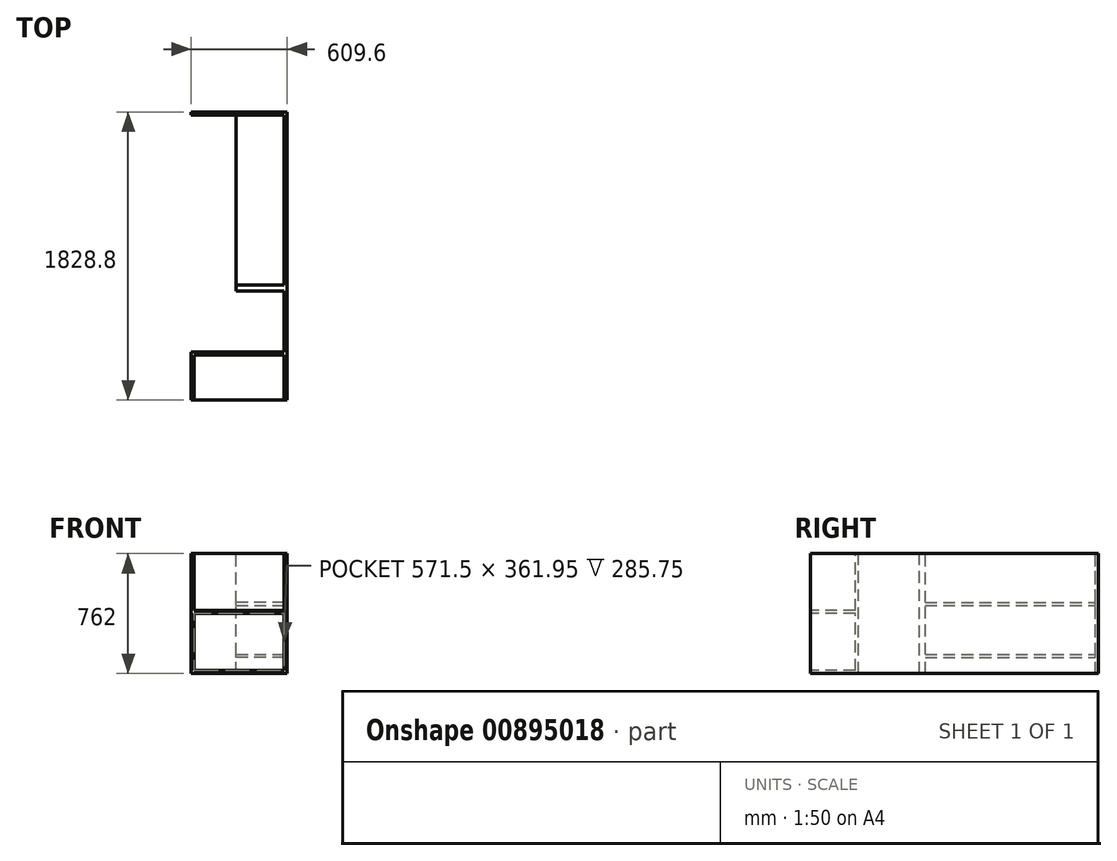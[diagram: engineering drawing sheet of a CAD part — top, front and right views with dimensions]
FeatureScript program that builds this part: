
annotation { "Feature Type Name" : "Feature", "Feature Type Description" : "" }
export const myFeature = defineFeature(function(context is Context, id is Id, definition is map)
    precondition{}
    {
        {
            var Q0;
            Q0=qCreatedBy(makeId("Front.planeOp"),FACE);
            var sketch = newSketch(context, id + "F0", { "sketchPlane" : qUnion([Q0])});
            skLineSegment(sketch, "E0.bottom", {"start": v(304.8, 381) * mm, "end": v(-304.8, 381) * mm});
            skLineSegment(sketch, "E0.top", {"start": v(304.8, -381) * mm, "end": v(-304.8, -381) * mm});
            skLineSegment(sketch, "E0.left", {"start": v(304.8, 381) * mm, "end": v(304.8, -381) * mm});
            skLineSegment(sketch, "E0.right", {"start": v(-304.8, 381) * mm, "end": v(-304.8, -381) * mm});
            skPoint(sketch, "E0.middle", {"position": v(0, 0) * mm});
            skSolve(sketch);
        }
        {
            var Q0;
            Q0=makeQuery(id+"F0.imprint","IMPRINT",FACE,{"disambiguationData":[TD([[makeQuery(id+"F0.imprint","IMPRINT",EDGE,{"derivedFrom":sQuery(id+"F0.wireOp",EDGE,"E0.bottom")}),1.0]])]});
            extrude(context, id + "F1", {"entities" : qUnion([Q0]), "depth" : 304.8 * mm, "offsetDistance" : 25.4 * mm});
        }
        {
            var Q0;
            Q0=makeQuery(id+"F1.opExtrude","CAP_FACE",FACE,{"disambiguationData":[OSD([sQuery(id+"F0.wireOp",EDGE,"E0.bottom"),sQuery(id+"F0.wireOp",EDGE,"E0.top"),sQuery(id+"F0.wireOp",EDGE,"E0.left"),sQuery(id+"F0.wireOp",EDGE,"E0.right")])],"isStart":false});
            var sketch = newSketch(context, id + "F2", { "sketchPlane" : qUnion([Q0])});
            skLineSegment(sketch, "E1.bottom", {"start": v(-285.75, 381) * mm, "end": v(285.75, 381) * mm});
            skLineSegment(sketch, "E1.top", {"start": v(-285.75, 19.05) * mm, "end": v(285.75, 19.05) * mm});
            skLineSegment(sketch, "E1.left", {"start": v(-285.75, 381) * mm, "end": v(-285.75, 19.05) * mm});
            skLineSegment(sketch, "E1.right", {"start": v(285.75, 381) * mm, "end": v(285.75, 19.05) * mm});
            skLineSegment(sketch, "E2.bottom", {"start": v(-285.75, 0) * mm, "end": v(285.75, 0) * mm});
            skLineSegment(sketch, "E2.top", {"start": v(-285.75, -361.95) * mm, "end": v(285.75, -361.95) * mm});
            skLineSegment(sketch, "E2.left", {"start": v(-285.75, 0) * mm, "end": v(-285.75, -361.95) * mm});
            skLineSegment(sketch, "E2.right", {"start": v(285.75, 0) * mm, "end": v(285.75, -361.95) * mm});
            skSolve(sketch);
        }
        {
            var Q0;
            Q0=makeQuery(id+"F2.imprint","IMPRINT",FACE,{"disambiguationData":[TD([[makeQuery(id+"F2.imprint","IMPRINT",EDGE,{"derivedFrom":sQuery(id+"F2.wireOp",EDGE,"E1.bottom")}),-1.0]])]});
            var Q1;
            Q1=makeQuery(id+"F2.imprint","IMPRINT",FACE,{"disambiguationData":[TD([[makeQuery(id+"F2.imprint","IMPRINT",EDGE,{"derivedFrom":sQuery(id+"F2.wireOp",EDGE,"E2.bottom")}),-1.0]])]});
            var Q2;
            Q2=makeQuery(id+"F2.imprint","IMPRINT",FACE,{"disambiguationData":[TD([[makeQuery(id+"F2.imprint","IMPRINT",EDGE,{"derivedFrom":sQuery(id+"F2.wireOp",EDGE,"E1.bottom")}),1.0]])]});
            var Q3;
            Q3=makeQuery(id+"F1.opExtrude","CAP_FACE",FACE,{"disambiguationData":[OSD([sQuery(id+"F0.wireOp",EDGE,"E0.bottom"),sQuery(id+"F0.wireOp",EDGE,"E0.top"),sQuery(id+"F0.wireOp",EDGE,"E0.left"),sQuery(id+"F0.wireOp",EDGE,"E0.right")])],"isStart":true});
            extrude(context, id + "F3", {"entities" : qUnion([Q0, Q1, Q2]), "operationType" : NewBodyOperationType.REMOVE, "endBound" : BoundingType.UP_TO_SURFACE, "oppositeDirection" : true, "depth" : 25.4 * mm, "endBoundEntityFace" : qUnion([Q3]), "hasOffset" : true, "offsetDistance" : 19.05 * mm});
        }
        {
            var Q0;
            Q0=makeQuery(id+"F1.opExtrude","SWEPT_FACE",FACE,{"disambiguationData":[OSD([sQuery(id+"F0.wireOp",EDGE,"E0.bottom")])]});
            var sketch = newSketch(context, id + "F4", { "sketchPlane" : qUnion([Q0])});
            skLineSegment(sketch, "E3", {"start": v(304.8, 0) * mm, "end": v(304.8, 1524) * mm});
            skLineSegment(sketch, "E4", {"start": v(304.8, 1524) * mm, "end": v(-304.8, 1524) * mm});
            skLineSegment(sketch, "E5", {"start": v(-304.8, 1524) * mm, "end": v(-304.8, 1504.95) * mm});
            skLineSegment(sketch, "E6", {"start": v(-304.8, 1504.95) * mm, "end": v(285.75, 1504.95) * mm});
            skLineSegment(sketch, "E7", {"start": v(285.75, 1504.95) * mm, "end": v(285.75, 425.45) * mm});
            skLineSegment(sketch, "E8.bottom", {"start": v(285.75, 387.35) * mm, "end": v(-19.05, 387.35) * mm});
            skLineSegment(sketch, "E8.top", {"start": v(285.75, 425.45) * mm, "end": v(-19.05, 425.45) * mm});
            skLineSegment(sketch, "E8.right", {"start": v(-19.05, 425.45) * mm, "end": v(-19.05, 387.35) * mm});
            skLineSegment(sketch, "E9.trimOffspring", {"start": v(285.75, 387.35) * mm, "end": v(285.75, 0) * mm});
            skSolve(sketch);
        }
        {
            var Q0;
            {var subQ0=sQuery(id+"F4.wireOp",EDGE,"E3");Q0=makeQuery(id+"F4.imprint","IMPRINT",FACE,{"disambiguationData":[TD([[makeQuery(id+"F4.imprint","IMPRINT",EDGE,{"derivedFrom":subQ0}),1.0]])]});}
            var Q1;
            Q1=makeQuery(id+"F1.opExtrude","SWEPT_FACE",FACE,{"disambiguationData":[OSD([sQuery(id+"F0.wireOp",EDGE,"E0.top")])]});
            extrude(context, id + "F5", {"entities" : qUnion([Q0]), "operationType" : NewBodyOperationType.ADD, "endBound" : BoundingType.UP_TO_SURFACE, "oppositeDirection" : true, "depth" : 25.4 * mm, "endBoundEntityFace" : qUnion([Q1]), "offsetDistance" : 25.4 * mm});
        }
        {
            var Q0;
            Q0=makeQuery(id+"F5.opExtrude","SWEPT_FACE",FACE,{"disambiguationData":[OSD([sQuery(id+"F4.wireOp",EDGE,"E6")])]});
            var sketch = newSketch(context, id + "F6", { "sketchPlane" : qUnion([Q0])});
            skLineSegment(sketch, "E10.bottom", {"start": v(285.75, -279.4) * mm, "end": v(-19.05, -279.4) * mm});
            skLineSegment(sketch, "E10.top", {"start": v(285.75, -260.35) * mm, "end": v(-19.05, -260.35) * mm});
            skLineSegment(sketch, "E10.left", {"start": v(285.75, -279.4) * mm, "end": v(285.75, -260.35) * mm});
            skLineSegment(sketch, "E10.right", {"start": v(-19.05, -279.4) * mm, "end": v(-19.05, -260.35) * mm});
            skLineSegment(sketch, "E11.bottom", {"start": v(285.75, 50.8) * mm, "end": v(-19.05, 50.8) * mm});
            skLineSegment(sketch, "E11.top", {"start": v(285.75, 69.85) * mm, "end": v(-19.05, 69.85) * mm});
            skLineSegment(sketch, "E11.left", {"start": v(285.75, 50.8) * mm, "end": v(285.75, 69.85) * mm});
            skLineSegment(sketch, "E11.right", {"start": v(-19.05, 50.8) * mm, "end": v(-19.05, 69.85) * mm});
            skLineSegment(sketch, "E12", {"start": v(285.75, -381) * mm, "end": v(285.75, -279.4) * mm, "construction": true});
            skLineSegment(sketch, "E13", {"start": v(285.75, -260.35) * mm, "end": v(285.75, 50.8) * mm, "construction": true});
            skLineSegment(sketch, "E14", {"start": v(285.75, 69.85) * mm, "end": v(285.75, 381) * mm, "construction": true});
            skSolve(sketch);
        }
        {
            var Q0;
            Q0 = qSketchRegion(id + "F6", true);
            var Q1;
            Q1=makeQuery(id+"F5.opExtrude","SWEPT_FACE",FACE,{"disambiguationData":[OSD([sQuery(id+"F4.wireOp",EDGE,"E8.top")])]});
            extrude(context, id + "F7", {"entities" : qUnion([Q0]), "operationType" : NewBodyOperationType.ADD, "endBound" : BoundingType.UP_TO_SURFACE, "depth" : 25.4 * mm, "endBoundEntityFace" : qUnion([Q1]), "offsetDistance" : 25.4 * mm});
        }
    });
